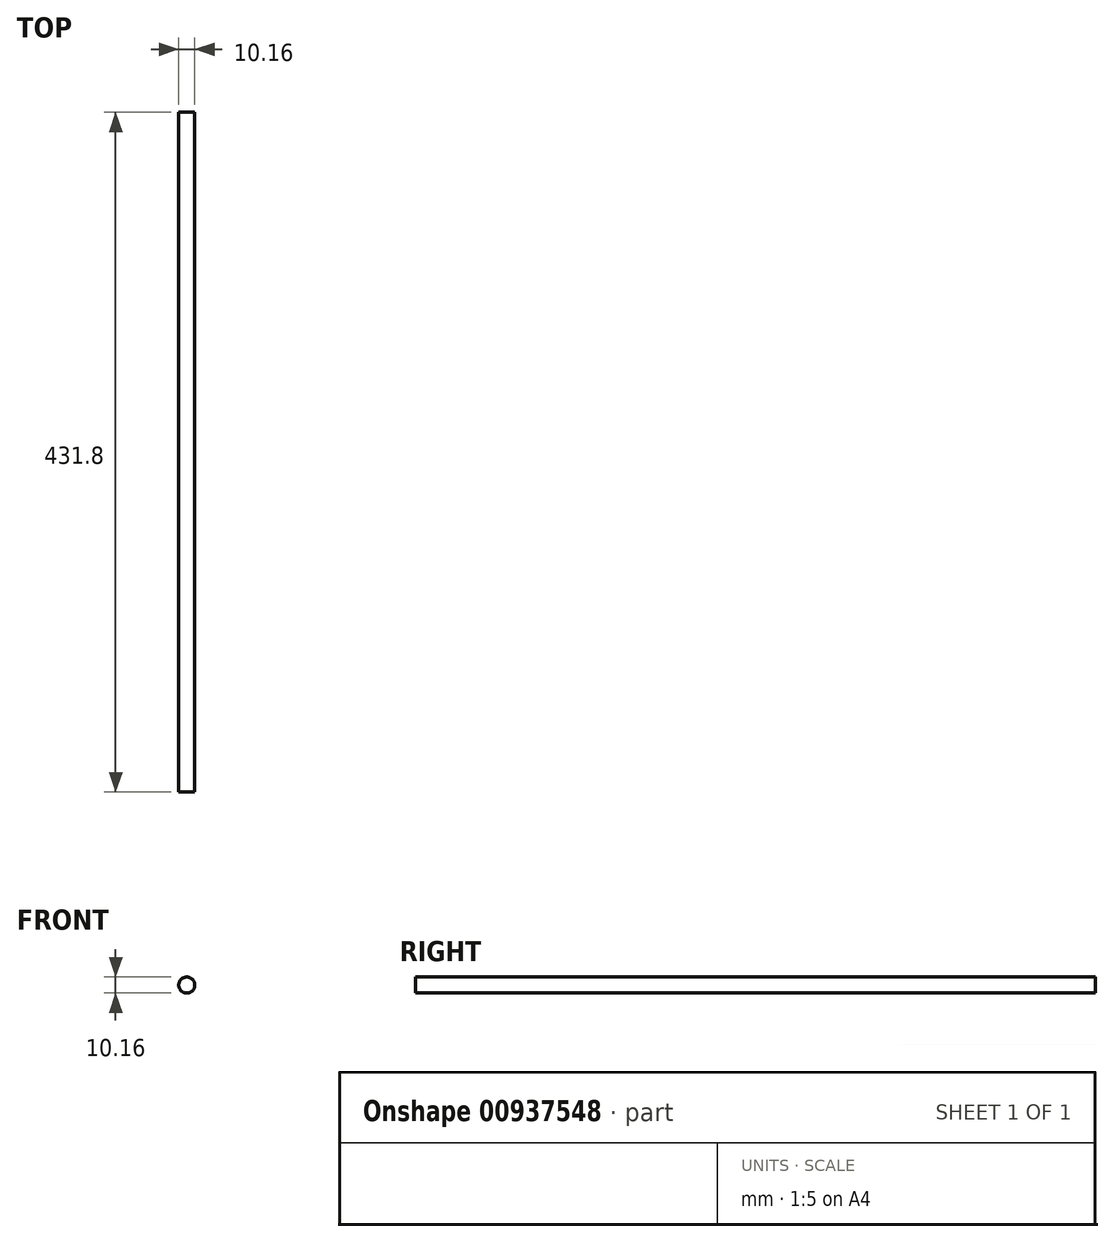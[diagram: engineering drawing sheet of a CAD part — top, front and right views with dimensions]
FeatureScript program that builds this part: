
annotation { "Feature Type Name" : "Feature", "Feature Type Description" : "" }
export const myFeature = defineFeature(function(context is Context, id is Id, definition is map)
    precondition{}
    {
        {
            var Q0;
            Q0=qCreatedBy(makeId("Front.planeOp"),FACE);
            var sketch = newSketch(context, id + "F0", { "sketchPlane" : qUnion([Q0])});
            skCircle(sketch, "E0", {"center": v(0, 0) * mm, "radius": 5.08 * mm});
            skSolve(sketch);
        }
        {
            var Q0;
            Q0 = qSketchRegion(id + "F0", true);
            extrude(context, id + "F1", {"entities" : qUnion([Q0]), "depth" : 431.8 * mm, "offsetDistance" : 25.4 * mm});
        }
    });
